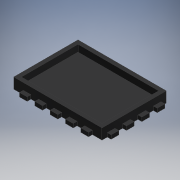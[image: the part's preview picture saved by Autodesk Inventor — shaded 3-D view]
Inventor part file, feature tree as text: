
AUTODESK INVENTOR PART (.ipt)
format: ipt  version: 2019 (Build 230136000, 136)  size: 224,768 bytes
history: native  units: mm
features: extrude x3, sketch x3, projected_geometry x1
ambient origin geometry x8: Origin, YZ Plane, XZ Plane, XY Plane, X Axis, Y Axis, Z Axis, Center Point
bodies: Solid1 (feature_tree)
feature tree (7):
  extrude  "Extrusion1"  Depth=75.0mm
  extrude  "Extrusion2"  Depth=4.0mm
  extrude  "Extrusion3"  Depth=7.0mm TaperAngle=0.0deg
  sketch  "Sketch1"  dims[d0=100.0mm d1=75.0mm]
  sketch  "Sketch2"  dims[d2=4.0mm d3=0.0mm d4=4.0mm]
  projected_geometry  "Projected Loop1"
  sketch  "Sketch3"  dims[d5=4.0mm d6=7.0mm d7=0.0mm d9=8.0mm d11=4.0mm d12=8.0mm d13=8.0mm d14=8.0mm d15=8.0mm d16=8.0mm d17=4.0mm d18=8.0mm d19=4.0mm d20=0.0mm]
